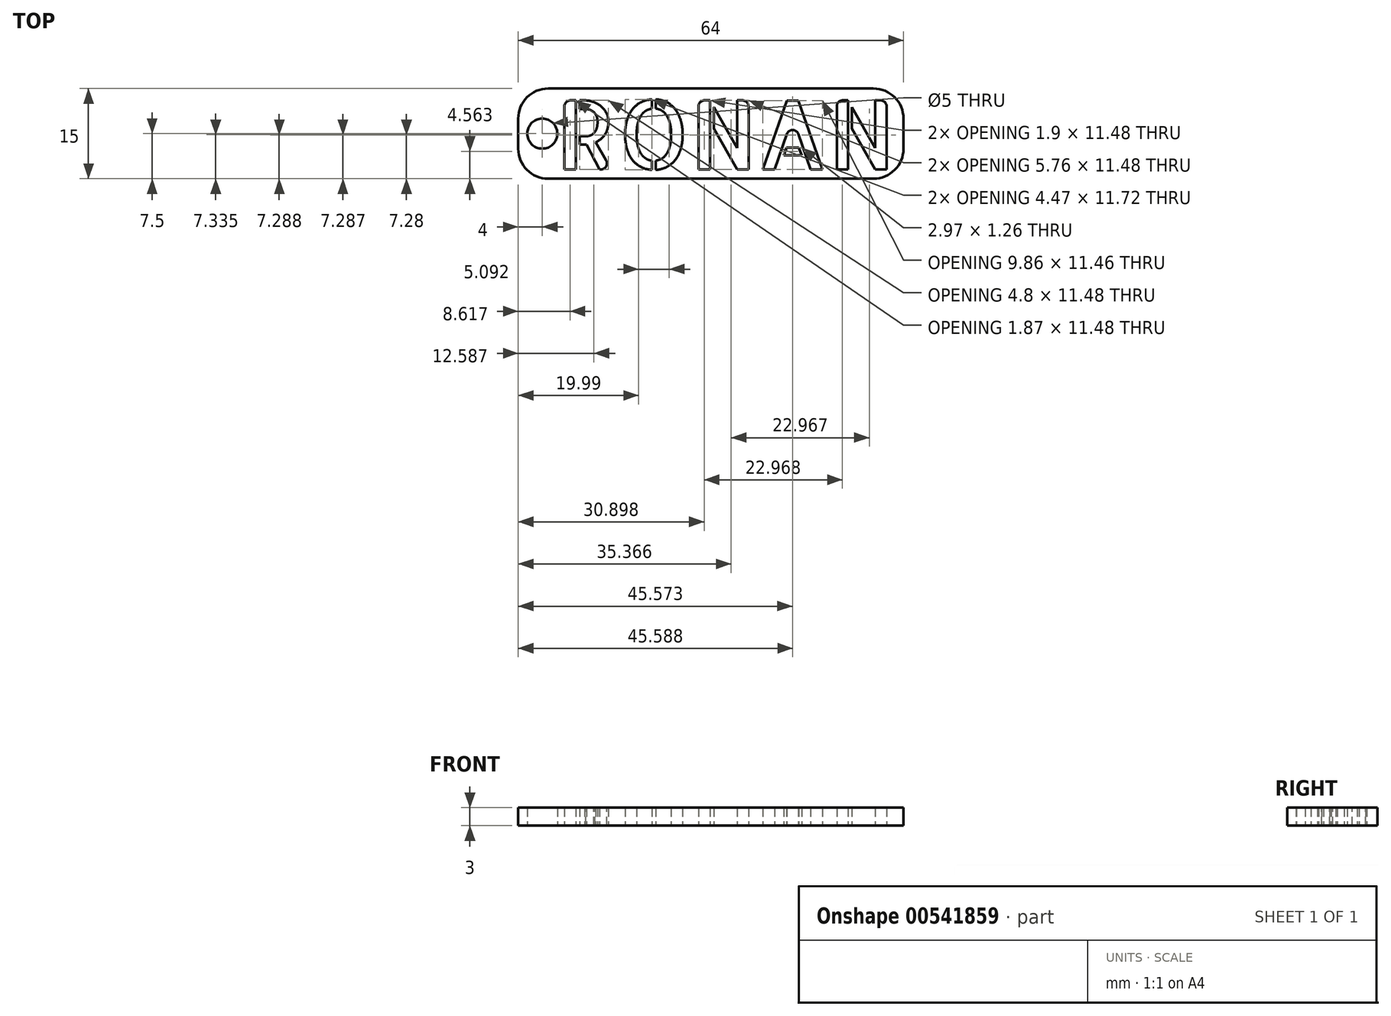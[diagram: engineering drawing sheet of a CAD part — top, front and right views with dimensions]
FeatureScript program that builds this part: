
annotation { "Feature Type Name" : "Feature", "Feature Type Description" : "" }
export const myFeature = defineFeature(function(context is Context, id is Id, definition is map)
    precondition{}
    {
        {
            var Q0;
            Q0=qCreatedBy(makeId("Top.planeOp"),FACE);
            var sketch = newSketch(context, id + "F0", { "sketchPlane" : qUnion([Q0])});
            skLineSegment(sketch, "E0.bottom", {"start": v(32, -7.5) * mm, "end": v(-32, -7.5) * mm});
            skLineSegment(sketch, "E0.top", {"start": v(32, 7.5) * mm, "end": v(-32, 7.5) * mm});
            skLineSegment(sketch, "E0.left", {"start": v(32, -7.5) * mm, "end": v(32, 7.5) * mm});
            skLineSegment(sketch, "E0.right", {"start": v(-32, -7.5) * mm, "end": v(-32, 7.5) * mm});
            skPoint(sketch, "E0.middle", {"position": v(0, 0) * mm});
            skText(sketch, "E1", { "text": "RONAN", "fontName": "AllertaStencil-Regular.ttf"});
            skLineSegment(sketch, "E2", {"start": v(-32, 0) * mm, "end": v(-28, 0) * mm});
            skPoint(sketch, "E2.endSnap0", {"position": v(-32, 0) * mm});
            skCircle(sketch, "E3", {"center": v(-28, 0) * mm, "radius": 2.5 * mm});
            const initialGuessF0  = {"E1": [-0.02572, -0.00595, 1, 0, 0.01148]};
            skSetInitialGuess(sketch, initialGuessF0);
            skSolve(sketch);
        }
        {
            var Q0;
            Q0 = qSketchRegion(id + "F0", true);
            extrude(context, id + "F1", {"entities" : qUnion([Q0]), "depth" : 3 * mm, "offsetDistance" : 25 * mm});
        }
        {
            var Q0;
            Q0=makeQuery(id+"F1.opExtrude","SWEPT_EDGE",EDGE,{"disambiguationData":[OSD([sQuery(id+"F0.wireOp",EDGE,"E0.bottom"),sQuery(id+"F0.wireOp",EDGE,"E0.right")])]});
            var Q1;
            Q1=makeQuery(id+"F1.opExtrude","SWEPT_EDGE",EDGE,{"disambiguationData":[OSD([sQuery(id+"F0.wireOp",EDGE,"E0.top"),sQuery(id+"F0.wireOp",EDGE,"E0.right")])]});
            var Q2;
            Q2=makeQuery(id+"F1.opExtrude","SWEPT_EDGE",EDGE,{"disambiguationData":[OSD([sQuery(id+"F0.wireOp",EDGE,"E0.top"),sQuery(id+"F0.wireOp",EDGE,"E0.left")])]});
            var Q3;
            Q3=makeQuery(id+"F1.opExtrude","SWEPT_EDGE",EDGE,{"disambiguationData":[OSD([sQuery(id+"F0.wireOp",EDGE,"E0.bottom"),sQuery(id+"F0.wireOp",EDGE,"E0.left")])]});
            fillet(context, id + "F2", {"entities" : qUnion([Q0, Q1, Q2, Q3]), "radius" : 5 * mm, "tangentPropagation" : true, "allowEdgeOverflow" : false});
        }
        {
            var Q0;
            Q0=makeQuery(id+"F1.opExtrude","SWEPT_EDGE",EDGE,{"disambiguationData":[OSD([sQuery(id+"F0.wireOp",EDGE,"E1.sketch_text.stroke-4"),sQuery(id+"F0.wireOp",EDGE,"E1.sketch_text.stroke-29")])]});
            var Q1;
            Q1=makeQuery(id+"F1.opExtrude","SWEPT_EDGE",EDGE,{"disambiguationData":[OSD([sQuery(id+"F0.wireOp",EDGE,"E1.sketch_text.stroke-88"),sQuery(id+"F0.wireOp",EDGE,"E1.sketch_text.stroke-89")])]});
            var Q2;
            Q2=makeQuery(id+"F1.opExtrude","SWEPT_EDGE",EDGE,{"disambiguationData":[OSD([sQuery(id+"F0.wireOp",EDGE,"E1.sketch_text.stroke-66"),sQuery(id+"F0.wireOp",EDGE,"E1.sketch_text.stroke-67")])]});
            var Q3;
            Q3=makeQuery(id+"F1.opExtrude","SWEPT_EDGE",EDGE,{"disambiguationData":[OSD([sQuery(id+"F0.wireOp",EDGE,"E1.sketch_text.stroke-78"),sQuery(id+"F0.wireOp",EDGE,"E1.sketch_text.stroke-79")])]});
            var Q4;
            Q4=makeQuery(id+"F1.opExtrude","SWEPT_EDGE",EDGE,{"disambiguationData":[OSD([sQuery(id+"F0.wireOp",EDGE,"E1.sketch_text.stroke-73"),sQuery(id+"F0.wireOp",EDGE,"E1.sketch_text.stroke-74")])]});
            var Q5;
            Q5=makeQuery(id+"F1.opExtrude","SWEPT_EDGE",EDGE,{"disambiguationData":[OSD([sQuery(id+"F0.wireOp",EDGE,"E1.sketch_text.stroke-95"),sQuery(id+"F0.wireOp",EDGE,"E1.sketch_text.stroke-96")])]});
            var Q6;
            Q6=makeQuery(id+"F1.opExtrude","SWEPT_EDGE",EDGE,{"disambiguationData":[OSD([sQuery(id+"F0.wireOp",EDGE,"E1.sketch_text.stroke-0"),sQuery(id+"F0.wireOp",EDGE,"E1.sketch_text.stroke-3")])]});
            fillet(context, id + "F3", {"entities" : qUnion([Q0, Q1, Q2, Q3, Q4, Q5, Q6]), "radius" : 1 * mm, "tangentPropagation" : true, "allowEdgeOverflow" : false});
        }
    });
